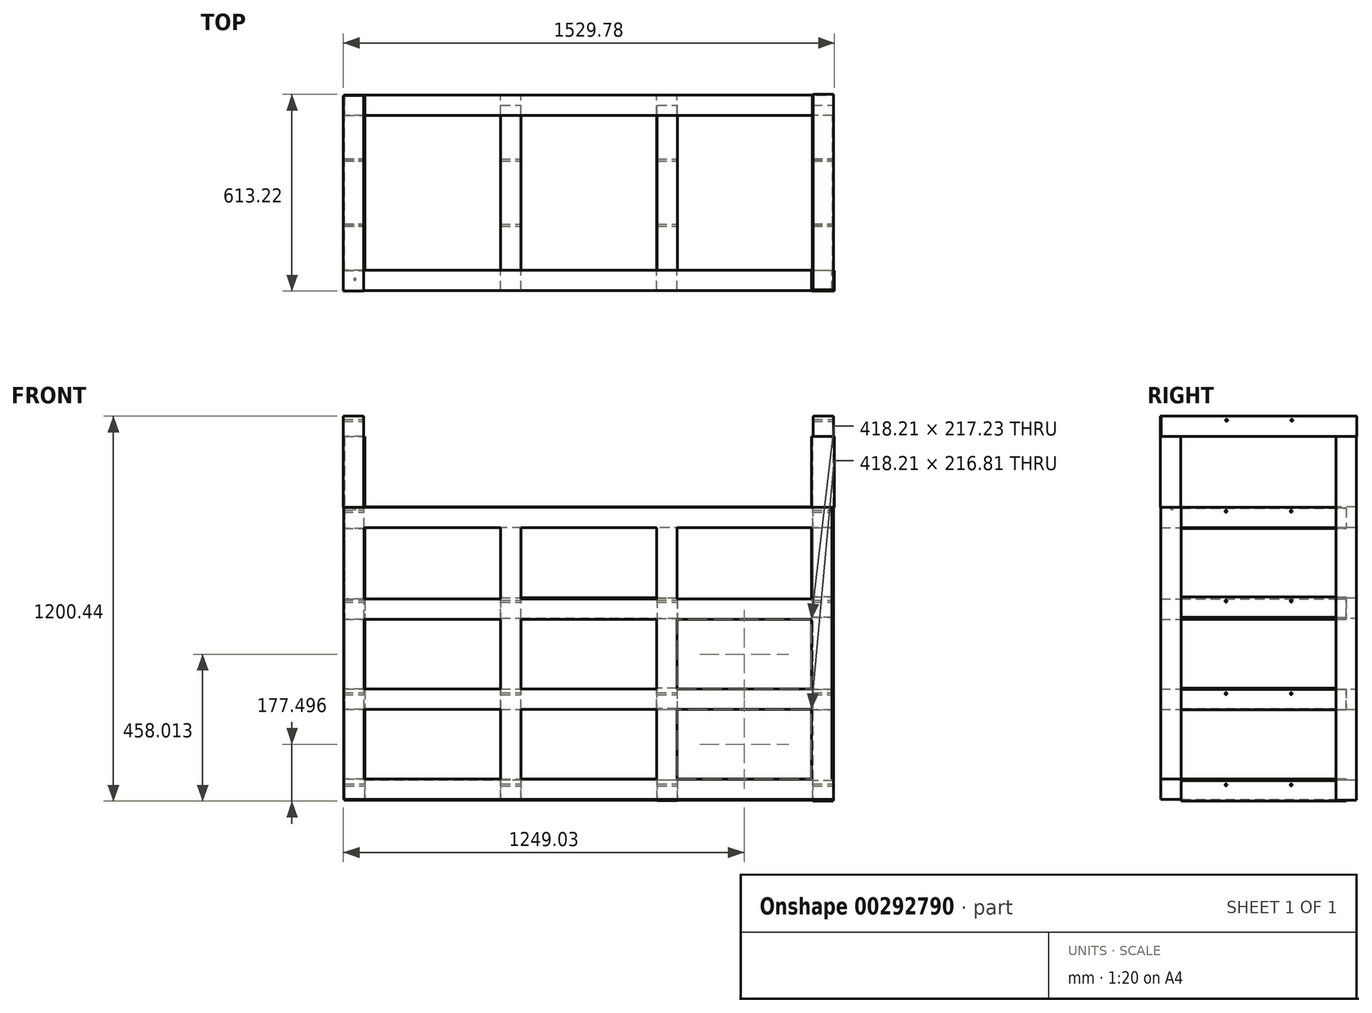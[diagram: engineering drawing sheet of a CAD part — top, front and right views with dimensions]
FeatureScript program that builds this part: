
annotation { "Feature Type Name" : "Feature", "Feature Type Description" : "" }
export const myFeature = defineFeature(function(context is Context, id is Id, definition is map)
    precondition{}
    {
        {
            var Q0;
            Q0=qCreatedBy(makeId("Front.planeOp"),FACE);
            var sketch = newSketch(context, id + "F0", { "sketchPlane" : qUnion([Q0])});
            skLineSegment(sketch, "E0.bottom", {"start": v(-550.42, 484.86) * mm, "end": v(-486.92, 484.86) * mm});
            skLineSegment(sketch, "E0.top", {"start": v(-550.42, -366.04) * mm, "end": v(-486.92, -366.04) * mm});
            skLineSegment(sketch, "E0.left", {"start": v(-550.42, 484.86) * mm, "end": v(-550.42, -366.04) * mm});
            skLineSegment(sketch, "E0.right", {"start": v(-486.92, 484.86) * mm, "end": v(-486.92, -366.04) * mm});
            skLineSegment(sketch, "E1.bottom", {"start": v(-486.92, -366.04) * mm, "end": v(910.08, -366.04) * mm});
            skLineSegment(sketch, "E1.top", {"start": v(-486.92, -302.54) * mm, "end": v(156.84, -302.54) * mm});
            skLineSegment(sketch, "E1.left", {"start": v(-486.92, -366.04) * mm, "end": v(-486.92, -302.54) * mm});
            skLineSegment(sketch, "E2.bottom", {"start": v(-550.42, 484.86) * mm, "end": v(973.58, 484.86) * mm});
            skLineSegment(sketch, "E2.top", {"start": v(-550.42, 548.36) * mm, "end": v(973.58, 548.36) * mm});
            skLineSegment(sketch, "E2.left", {"start": v(-550.42, 484.86) * mm, "end": v(-550.42, 548.36) * mm});
            skLineSegment(sketch, "E2.right", {"start": v(973.58, 484.86) * mm, "end": v(973.58, 548.36) * mm});
            skLineSegment(sketch, "E3.bottom", {"start": v(910.08, -366.04) * mm, "end": v(973.58, -366.04) * mm});
            skLineSegment(sketch, "E3.top", {"start": v(910.08, 484.86) * mm, "end": v(973.58, 484.86) * mm});
            skLineSegment(sketch, "E3.left", {"start": v(910.08, -366.04) * mm, "end": v(910.08, 484.86) * mm});
            skLineSegment(sketch, "E3.right", {"start": v(973.58, -366.04) * mm, "end": v(973.58, 484.86) * mm});
            skLineSegment(sketch, "E4", {"start": v(156.84, -302.54) * mm, "end": v(910.08, -302.54) * mm});
            skLineSegment(sketch, "E5.bottom", {"start": v(-486.92, 201.14) * mm, "end": v(910.08, 201.14) * mm});
            skLineSegment(sketch, "E5.top", {"start": v(-486.92, 264.64) * mm, "end": v(910.08, 264.64) * mm});
            skLineSegment(sketch, "E5.left", {"start": v(-486.92, 264.64) * mm, "end": v(-486.92, 201.14) * mm});
            skLineSegment(sketch, "E5.right", {"start": v(910.08, 264.64) * mm, "end": v(910.08, 201.14) * mm});
            skLineSegment(sketch, "E6.bottom", {"start": v(-486.92, -82.58) * mm, "end": v(910.08, -82.58) * mm});
            skLineSegment(sketch, "E6.top", {"start": v(-486.92, -19.08) * mm, "end": v(910.08, -19.08) * mm});
            skLineSegment(sketch, "E6.left", {"start": v(-486.92, -82.58) * mm, "end": v(-486.92, -19.08) * mm});
            skLineSegment(sketch, "E6.right", {"start": v(910.08, -82.58) * mm, "end": v(910.08, -19.08) * mm});
            skLineSegment(sketch, "E7.bottom", {"start": v(-63.5, 484.86) * mm, "end": v(0, 484.86) * mm});
            skLineSegment(sketch, "E7.top", {"start": v(-63.5, -302.54) * mm, "end": v(0, -302.54) * mm});
            skLineSegment(sketch, "E7.left", {"start": v(-63.5, 484.86) * mm, "end": v(-63.5, -302.54) * mm});
            skLineSegment(sketch, "E7.right", {"start": v(0, 484.86) * mm, "end": v(0, -302.54) * mm});
            skLineSegment(sketch, "E8.bottom", {"start": v(423.42, 484.86) * mm, "end": v(486.92, 484.86) * mm});
            skLineSegment(sketch, "E8.top", {"start": v(423.42, -302.54) * mm, "end": v(486.92, -302.54) * mm});
            skLineSegment(sketch, "E8.left", {"start": v(423.42, 484.86) * mm, "end": v(423.42, -302.54) * mm});
            skLineSegment(sketch, "E8.right", {"start": v(486.92, 484.86) * mm, "end": v(486.92, -302.54) * mm});
            skSolve(sketch);
        }
        {
            var Q0;
            Q0=makeQuery(id+"F0.imprint","IMPRINT",FACE,{"disambiguationData":[TD([[makeQuery(id+"F0.imprint","IMPRINT",EDGE,{"derivedFrom":sQuery(id+"F0.wireOp",EDGE,"E0.top")}),1.0]])]});
            var Q1;
            {var subQ0=sQuery(id+"F0.wireOp",EDGE,"E6.left");Q1=makeQuery(id+"F0.imprint","IMPRINT",FACE,{"disambiguationData":[TD([[makeQuery(id+"F0.imprint","IMPRINT",EDGE,{"derivedFrom":subQ0}),-1.0]])]});}
            var Q2;
            {var subQ0=sQuery(id+"F0.wireOp",EDGE,"E7.right");var subQ1=sQuery(id+"F0.wireOp",EDGE,"E6.bottom");var subQ2=makeQuery(id+"F0.imprint","INTERSECT",VERTEX,{"derivedFrom":[subQ1,subQ0]});Q2=makeQuery(id+"F0.imprint","IMPRINT",FACE,{"disambiguationData":[TD([[makeQuery(id+"F0.imprint","IMPRINT",EDGE,{"disambiguationData":[TD([[subQ2,-1.0]])],"derivedFrom":subQ1}),1.0]])]});}
            var Q3;
            {var subQ0=sQuery(id+"F0.wireOp",EDGE,"E6.right");Q3=makeQuery(id+"F0.imprint","IMPRINT",FACE,{"disambiguationData":[TD([[makeQuery(id+"F0.imprint","IMPRINT",EDGE,{"derivedFrom":subQ0}),1.0]])]});}
            var Q4;
            {var subQ5=sQuery(id+"F0.wireOp",EDGE,"E8.top");Q4=makeQuery(id+"F0.imprint","IMPRINT",FACE,{"disambiguationData":[TD([[makeQuery(id+"F0.imprint","IMPRINT",EDGE,{"derivedFrom":subQ5}),1.0]])]});}
            var Q5;
            {var subQ0=sQuery(id+"F0.wireOp",EDGE,"E8.left");var subQ1=sQuery(id+"F0.wireOp",EDGE,"E6.bottom");var subQ2=makeQuery(id+"F0.imprint","INTERSECT",VERTEX,{"derivedFrom":[subQ1,subQ0]});Q5=makeQuery(id+"F0.imprint","IMPRINT",FACE,{"disambiguationData":[TD([[makeQuery(id+"F0.imprint","IMPRINT",EDGE,{"disambiguationData":[TD([[subQ2,-1.0]])],"derivedFrom":subQ1}),1.0]])]});}
            var Q6;
            {var subQ0=sQuery(id+"F0.wireOp",EDGE,"E8.left");var subQ1=sQuery(id+"F0.wireOp",EDGE,"E5.bottom");var subQ2=makeQuery(id+"F0.imprint","INTERSECT",VERTEX,{"derivedFrom":[subQ1,subQ0]});Q6=makeQuery(id+"F0.imprint","IMPRINT",FACE,{"disambiguationData":[TD([[makeQuery(id+"F0.imprint","IMPRINT",EDGE,{"disambiguationData":[TD([[subQ2,-1.0]])],"derivedFrom":subQ1}),-1.0]])]});}
            var Q7;
            {var subQ0=sQuery(id+"F0.wireOp",EDGE,"E8.left");var subQ1=sQuery(id+"F0.wireOp",EDGE,"E5.bottom");var subQ2=makeQuery(id+"F0.imprint","INTERSECT",VERTEX,{"derivedFrom":[subQ1,subQ0]});Q7=makeQuery(id+"F0.imprint","IMPRINT",FACE,{"disambiguationData":[TD([[makeQuery(id+"F0.imprint","IMPRINT",EDGE,{"disambiguationData":[TD([[subQ2,-1.0]])],"derivedFrom":subQ1}),1.0]])]});}
            var Q8;
            {var subQ5=sQuery(id+"F0.wireOp",EDGE,"E8.bottom");Q8=makeQuery(id+"F0.imprint","IMPRINT",FACE,{"disambiguationData":[TD([[makeQuery(id+"F0.imprint","IMPRINT",EDGE,{"derivedFrom":subQ5}),-1.0]])]});}
            var Q9;
            {var subQ0=sQuery(id+"F0.wireOp",EDGE,"E7.right");var subQ1=sQuery(id+"F0.wireOp",EDGE,"E5.bottom");var subQ2=makeQuery(id+"F0.imprint","INTERSECT",VERTEX,{"derivedFrom":[subQ1,subQ0]});Q9=makeQuery(id+"F0.imprint","IMPRINT",FACE,{"disambiguationData":[TD([[makeQuery(id+"F0.imprint","IMPRINT",EDGE,{"disambiguationData":[TD([[subQ2,-1.0]])],"derivedFrom":subQ1}),1.0]])]});}
            var Q10;
            {var subQ5=sQuery(id+"F0.wireOp",EDGE,"E7.bottom");Q10=makeQuery(id+"F0.imprint","IMPRINT",FACE,{"disambiguationData":[TD([[makeQuery(id+"F0.imprint","IMPRINT",EDGE,{"derivedFrom":subQ5}),-1.0]])]});}
            var Q11;
            {var subQ0=sQuery(id+"F0.wireOp",EDGE,"E7.left");var subQ1=sQuery(id+"F0.wireOp",EDGE,"E5.bottom");var subQ2=makeQuery(id+"F0.imprint","INTERSECT",VERTEX,{"derivedFrom":[subQ1,subQ0]});Q11=makeQuery(id+"F0.imprint","IMPRINT",FACE,{"disambiguationData":[TD([[makeQuery(id+"F0.imprint","IMPRINT",EDGE,{"disambiguationData":[TD([[subQ2,-1.0]])],"derivedFrom":subQ1}),-1.0]])]});}
            var Q12;
            {var subQ0=sQuery(id+"F0.wireOp",EDGE,"E7.left");var subQ1=sQuery(id+"F0.wireOp",EDGE,"E6.bottom");var subQ2=makeQuery(id+"F0.imprint","INTERSECT",VERTEX,{"derivedFrom":[subQ1,subQ0]});Q12=makeQuery(id+"F0.imprint","IMPRINT",FACE,{"disambiguationData":[TD([[makeQuery(id+"F0.imprint","IMPRINT",EDGE,{"disambiguationData":[TD([[subQ2,-1.0]])],"derivedFrom":subQ1}),1.0]])]});}
            var Q13;
            {var subQ5=sQuery(id+"F0.wireOp",EDGE,"E7.top");Q13=makeQuery(id+"F0.imprint","IMPRINT",FACE,{"disambiguationData":[TD([[makeQuery(id+"F0.imprint","IMPRINT",EDGE,{"derivedFrom":subQ5}),1.0]])]});}
            var Q14;
            {var subQ0=sQuery(id+"F0.wireOp",EDGE,"E5.left");Q14=makeQuery(id+"F0.imprint","IMPRINT",FACE,{"disambiguationData":[TD([[makeQuery(id+"F0.imprint","IMPRINT",EDGE,{"derivedFrom":subQ0}),1.0]])]});}
            var Q15;
            {var subQ0=sQuery(id+"F0.wireOp",EDGE,"E7.left");var subQ1=sQuery(id+"F0.wireOp",EDGE,"E5.bottom");var subQ2=makeQuery(id+"F0.imprint","INTERSECT",VERTEX,{"derivedFrom":[subQ1,subQ0]});Q15=makeQuery(id+"F0.imprint","IMPRINT",FACE,{"disambiguationData":[TD([[makeQuery(id+"F0.imprint","IMPRINT",EDGE,{"disambiguationData":[TD([[subQ2,-1.0]])],"derivedFrom":subQ1}),1.0]])]});}
            var Q16;
            {var subQ0=sQuery(id+"F0.wireOp",EDGE,"E5.right");Q16=makeQuery(id+"F0.imprint","IMPRINT",FACE,{"disambiguationData":[TD([[makeQuery(id+"F0.imprint","IMPRINT",EDGE,{"derivedFrom":subQ0}),-1.0]])]});}
            var Q17;
            {var subQ3=sQuery(id+"F0.wireOp",EDGE,"E3.bottom");Q17=makeQuery(id+"F0.imprint","IMPRINT",FACE,{"disambiguationData":[TD([[makeQuery(id+"F0.imprint","IMPRINT",EDGE,{"derivedFrom":subQ3}),1.0]])]});}
            var Q18;
            {var subQ6=sQuery(id+"F0.wireOp",EDGE,"E1.bottom");Q18=makeQuery(id+"F0.imprint","IMPRINT",FACE,{"disambiguationData":[TD([[makeQuery(id+"F0.imprint","IMPRINT",EDGE,{"derivedFrom":subQ6}),1.0]])]});}
            extrude(context, id + "F1", {"entities" : qUnion([Q0, Q1, Q2, Q3, Q4, Q5, Q6, Q7, Q8, Q9, Q10, Q11, Q12, Q13, Q14, Q15, Q16, Q17, Q18]), "endBound" : BoundingType.SYMMETRIC, "depth" : 63.5 * mm});
        }
        {
            var Q0;
            Q0=makeQuery(id+"F0.imprint","IMPRINT",FACE,{"disambiguationData":[TD([[makeQuery(id+"F0.imprint","IMPRINT",EDGE,{"derivedFrom":sQuery(id+"F0.wireOp",EDGE,"E2.top")}),-1.0]])]});
            extrude(context, id + "F2", {"entities" : qUnion([Q0]), "operationType" : NewBodyOperationType.ADD, "endBound" : BoundingType.SYMMETRIC, "oppositeDirection" : true, "depth" : 63.5 * mm});
        }
        {
            var Q0;
            {var subQ0=sQuery(id+"F0.wireOp",EDGE,"E2.bottom");var subQ1=sQuery(id+"F0.wireOp",EDGE,"E0.right");var subQ2=makeQuery(id+"F0.imprint","INTERSECT",VERTEX,{"derivedFrom":[subQ1,subQ0]});Q0=makeQuery(id+"F0.imprint","IMPRINT",FACE,{"disambiguationData":[TD([[makeQuery(id+"F0.imprint","IMPRINT",EDGE,{"disambiguationData":[TD([[subQ2,-1.0]])],"derivedFrom":subQ1}),1.0]])]});}
            var sketch = newSketch(context, id + "F3", { "sketchPlane" : qUnion([Q0])});
            skLineSegment(sketch, "E9.bottom", {"start": v(-552.6, 544.64) * mm, "end": v(-489.1, 544.64) * mm});
            skLineSegment(sketch, "E9.top", {"start": v(-552.6, 481.14) * mm, "end": v(-489.1, 481.14) * mm});
            skLineSegment(sketch, "E9.left", {"start": v(-552.6, 544.64) * mm, "end": v(-552.6, 481.14) * mm});
            skLineSegment(sketch, "E9.right", {"start": v(-489.1, 544.64) * mm, "end": v(-489.1, 481.14) * mm});
            skLineSegment(sketch, "E10.bottom", {"start": v(-489.1, 260.92) * mm, "end": v(-552.6, 260.92) * mm});
            skLineSegment(sketch, "E10.top", {"start": v(-489.1, 197.42) * mm, "end": v(-552.6, 197.42) * mm});
            skLineSegment(sketch, "E10.left", {"start": v(-489.1, 260.92) * mm, "end": v(-489.1, 197.42) * mm});
            skLineSegment(sketch, "E10.right", {"start": v(-552.6, 260.92) * mm, "end": v(-552.6, 197.42) * mm});
            skLineSegment(sketch, "E11.bottom", {"start": v(-63.5, -82.58) * mm, "end": v(0, -82.58) * mm});
            skLineSegment(sketch, "E11.top", {"start": v(-63.5, -19.08) * mm, "end": v(0, -19.08) * mm});
            skLineSegment(sketch, "E11.left", {"start": v(-63.5, -82.58) * mm, "end": v(-63.5, -19.08) * mm});
            skLineSegment(sketch, "E11.right", {"start": v(0, -82.58) * mm, "end": v(0, -19.08) * mm});
            skLineSegment(sketch, "E12.bottom", {"start": v(-63.5, 201.14) * mm, "end": v(0, 201.14) * mm});
            skLineSegment(sketch, "E12.top", {"start": v(-63.5, 264.64) * mm, "end": v(0, 264.64) * mm});
            skLineSegment(sketch, "E12.left", {"start": v(-63.5, 201.14) * mm, "end": v(-63.5, 264.64) * mm});
            skLineSegment(sketch, "E12.right", {"start": v(0, 201.14) * mm, "end": v(0, 264.64) * mm});
            skLineSegment(sketch, "E13.bottom", {"start": v(-549.58, -363.18) * mm, "end": v(-486.08, -363.18) * mm});
            skLineSegment(sketch, "E13.top", {"start": v(-549.58, -299.68) * mm, "end": v(-486.08, -299.68) * mm});
            skLineSegment(sketch, "E13.left", {"start": v(-549.58, -363.18) * mm, "end": v(-549.58, -299.68) * mm});
            skLineSegment(sketch, "E13.right", {"start": v(-486.08, -363.18) * mm, "end": v(-486.08, -299.68) * mm});
            skLineSegment(sketch, "E14.bottom", {"start": v(-63.5, -299.68) * mm, "end": v(0, -299.68) * mm});
            skLineSegment(sketch, "E14.top", {"start": v(-63.5, -363.18) * mm, "end": v(0, -363.18) * mm});
            skLineSegment(sketch, "E14.left", {"start": v(-63.5, -299.68) * mm, "end": v(-63.5, -363.18) * mm});
            skLineSegment(sketch, "E14.right", {"start": v(0, -299.68) * mm, "end": v(0, -363.18) * mm});
            skLineSegment(sketch, "E15.bottom", {"start": v(909.19, -305.71) * mm, "end": v(972.69, -305.71) * mm});
            skLineSegment(sketch, "E15.top", {"start": v(909.19, -369.21) * mm, "end": v(972.69, -369.21) * mm});
            skLineSegment(sketch, "E15.left", {"start": v(909.19, -305.71) * mm, "end": v(909.19, -369.21) * mm});
            skLineSegment(sketch, "E15.right", {"start": v(972.69, -305.71) * mm, "end": v(972.69, -369.21) * mm});
            skLineSegment(sketch, "E16.bottom", {"start": v(909.19, 483.75) * mm, "end": v(972.69, 483.75) * mm});
            skLineSegment(sketch, "E16.top", {"start": v(909.19, 547.25) * mm, "end": v(972.69, 547.25) * mm});
            skLineSegment(sketch, "E16.left", {"start": v(909.19, 483.75) * mm, "end": v(909.19, 547.25) * mm});
            skLineSegment(sketch, "E16.right", {"start": v(972.69, 483.75) * mm, "end": v(972.69, 547.25) * mm});
            skLineSegment(sketch, "E17.bottom", {"start": v(-489.32, -19.28) * mm, "end": v(-552.82, -19.28) * mm});
            skLineSegment(sketch, "E17.top", {"start": v(-489.32, -82.78) * mm, "end": v(-552.82, -82.78) * mm});
            skLineSegment(sketch, "E17.left", {"start": v(-489.32, -19.28) * mm, "end": v(-489.32, -82.78) * mm});
            skLineSegment(sketch, "E17.right", {"start": v(-552.82, -19.28) * mm, "end": v(-552.82, -82.78) * mm});
            skLineSegment(sketch, "E18.bottom", {"start": v(486.58, -17.47) * mm, "end": v(423.42, -17.47) * mm});
            skLineSegment(sketch, "E18.top", {"start": v(486.58, -80.97) * mm, "end": v(423.42, -80.97) * mm});
            skLineSegment(sketch, "E18.left", {"start": v(486.58, -17.47) * mm, "end": v(486.58, -80.97) * mm});
            skLineSegment(sketch, "E18.right", {"start": v(423.42, -17.47) * mm, "end": v(423.42, -80.97) * mm});
            skLineSegment(sketch, "E19.bottom", {"start": v(908.2, -21.08) * mm, "end": v(971.7, -21.08) * mm});
            skLineSegment(sketch, "E19.top", {"start": v(908.2, -84.58) * mm, "end": v(971.7, -84.58) * mm});
            skLineSegment(sketch, "E19.left", {"start": v(908.2, -21.08) * mm, "end": v(908.2, -84.58) * mm});
            skLineSegment(sketch, "E19.right", {"start": v(971.7, -21.08) * mm, "end": v(971.7, -84.58) * mm});
            skLineSegment(sketch, "E20.bottom", {"start": v(424.17, -303.6) * mm, "end": v(487.67, -303.6) * mm});
            skLineSegment(sketch, "E20.top", {"start": v(424.17, -367.1) * mm, "end": v(487.67, -367.1) * mm});
            skLineSegment(sketch, "E20.left", {"start": v(424.17, -303.6) * mm, "end": v(424.17, -367.1) * mm});
            skLineSegment(sketch, "E20.right", {"start": v(487.67, -303.6) * mm, "end": v(487.67, -367.1) * mm});
            skLineSegment(sketch, "E21.bottom", {"start": v(487.12, 263.7) * mm, "end": v(423.62, 263.7) * mm});
            skLineSegment(sketch, "E21.top", {"start": v(487.12, 200.2) * mm, "end": v(423.62, 200.2) * mm});
            skLineSegment(sketch, "E21.left", {"start": v(487.12, 263.7) * mm, "end": v(487.12, 200.2) * mm});
            skLineSegment(sketch, "E21.right", {"start": v(423.62, 263.7) * mm, "end": v(423.62, 200.2) * mm});
            skLineSegment(sketch, "E22.bottom", {"start": v(908.58, 267.37) * mm, "end": v(972.08, 267.37) * mm});
            skLineSegment(sketch, "E22.top", {"start": v(908.58, 203.87) * mm, "end": v(972.08, 203.87) * mm});
            skLineSegment(sketch, "E22.left", {"start": v(908.58, 267.37) * mm, "end": v(908.58, 203.87) * mm});
            skLineSegment(sketch, "E22.right", {"start": v(972.08, 267.37) * mm, "end": v(972.08, 203.87) * mm});
            skSolve(sketch);
        }
        {
            var Q0;
            Q0 = qSketchRegion(id + "F3", true);
            extrude(context, id + "F4", {"entities" : qUnion([Q0]), "operationType" : NewBodyOperationType.ADD, "depth" : 514.35 * mm});
        }
        {
            var Q0;
            Q0=makeQuery(id+"F4.opExtrude","CAP_FACE",FACE,{"disambiguationData":[OSD([sQuery(id+"F3.wireOp",EDGE,"E10.bottom"),sQuery(id+"F3.wireOp",EDGE,"E10.top"),sQuery(id+"F3.wireOp",EDGE,"E10.left"),sQuery(id+"F3.wireOp",EDGE,"E10.right")])],"isStart":false});
            var sketch = newSketch(context, id + "F5", { "sketchPlane" : qUnion([Q0])});
            skLineSegment(sketch, "E23.bottom", {"start": v(-552.6, 197.42) * mm, "end": v(968.4, 197.42) * mm});
            skLineSegment(sketch, "E23.top", {"start": v(-552.6, 260.92) * mm, "end": v(968.4, 260.92) * mm});
            skLineSegment(sketch, "E23.left", {"start": v(-552.6, 197.42) * mm, "end": v(-552.6, 260.92) * mm});
            skLineSegment(sketch, "E23.right", {"start": v(968.4, 197.42) * mm, "end": v(968.4, 260.92) * mm});
            skLineSegment(sketch, "E24.bottom", {"start": v(-552.6, 547.51) * mm, "end": v(968.4, 547.51) * mm});
            skLineSegment(sketch, "E24.top", {"start": v(-552.6, 484.01) * mm, "end": v(968.4, 484.01) * mm});
            skLineSegment(sketch, "E24.left", {"start": v(-552.6, 547.51) * mm, "end": v(-552.6, 484.01) * mm});
            skLineSegment(sketch, "E24.right", {"start": v(968.4, 547.51) * mm, "end": v(968.4, 484.01) * mm});
            skLineSegment(sketch, "E25.bottom", {"start": v(-552.6, -83.31) * mm, "end": v(968.4, -83.31) * mm});
            skLineSegment(sketch, "E25.top", {"start": v(-552.6, -19.81) * mm, "end": v(968.4, -19.81) * mm});
            skLineSegment(sketch, "E25.left", {"start": v(-552.6, -83.31) * mm, "end": v(-552.6, -19.81) * mm});
            skLineSegment(sketch, "E25.right", {"start": v(968.4, -83.31) * mm, "end": v(968.4, -19.81) * mm});
            skLineSegment(sketch, "E26.bottom", {"start": v(-549.97, -363.62) * mm, "end": v(974.09, -363.62) * mm});
            skLineSegment(sketch, "E26.top", {"start": v(-549.97, -300.12) * mm, "end": v(974.09, -300.12) * mm});
            skLineSegment(sketch, "E26.left", {"start": v(-549.97, -363.62) * mm, "end": v(-549.97, -300.12) * mm});
            skLineSegment(sketch, "E26.right", {"start": v(974.09, -363.62) * mm, "end": v(974.09, -300.12) * mm});
            skLineSegment(sketch, "E27.bottom", {"start": v(-552.6, 547.51) * mm, "end": v(-489.1, 547.51) * mm});
            skLineSegment(sketch, "E27.top", {"start": v(-552.6, -363.62) * mm, "end": v(-489.1, -363.62) * mm});
            skLineSegment(sketch, "E27.left", {"start": v(-552.6, 547.51) * mm, "end": v(-552.6, -363.62) * mm});
            skLineSegment(sketch, "E27.right", {"start": v(-489.1, 547.51) * mm, "end": v(-489.1, -363.62) * mm});
            skLineSegment(sketch, "E28.bottom", {"start": v(-63.5, -363.62) * mm, "end": v(0, -363.62) * mm});
            skLineSegment(sketch, "E28.top", {"start": v(-63.5, 547.51) * mm, "end": v(0, 547.51) * mm});
            skLineSegment(sketch, "E28.left", {"start": v(-63.5, -363.62) * mm, "end": v(-63.5, 547.51) * mm});
            skLineSegment(sketch, "E28.right", {"start": v(0, -363.62) * mm, "end": v(0, 547.51) * mm});
            skLineSegment(sketch, "E29.bottom", {"start": v(423.2, -363.62) * mm, "end": v(486.7, -363.62) * mm});
            skLineSegment(sketch, "E29.top", {"start": v(423.2, 547.51) * mm, "end": v(486.7, 547.51) * mm});
            skLineSegment(sketch, "E29.left", {"start": v(423.2, -363.62) * mm, "end": v(423.2, 547.51) * mm});
            skLineSegment(sketch, "E29.right", {"start": v(486.7, -363.62) * mm, "end": v(486.7, 547.51) * mm});
            skLineSegment(sketch, "E30.bottom", {"start": v(904.9, -363.62) * mm, "end": v(968.4, -363.62) * mm});
            skLineSegment(sketch, "E30.top", {"start": v(904.9, 547.51) * mm, "end": v(968.4, 547.51) * mm});
            skLineSegment(sketch, "E30.left", {"start": v(904.9, -363.62) * mm, "end": v(904.9, 547.51) * mm});
            skLineSegment(sketch, "E30.right", {"start": v(968.4, -363.62) * mm, "end": v(968.4, 547.51) * mm});
            skSolve(sketch);
        }
        {
            var Q0;
            Q0 = qSketchRegion(id + "F5", true);
            var Q1;
            {var subQ0=sQuery(id+"F5.wireOp",EDGE,"E23.top");var subQ1=sQuery(id+"F5.wireOp",EDGE,"E27.right");var subQ2=makeQuery(id+"F5.imprint","INTERSECT",VERTEX,{"derivedFrom":[subQ1,subQ0]});Q1=makeQuery(id+"F5.imprint","IMPRINT",FACE,{"disambiguationData":[TD([[makeQuery(id+"F5.imprint","IMPRINT",EDGE,{"disambiguationData":[TD([[subQ2,-1.0]])],"derivedFrom":subQ1}),1.0]])]});}
            var Q2;
            {var subQ0=sQuery(id+"F5.wireOp",EDGE,"E23.bottom");var subQ1=sQuery(id+"F5.wireOp",EDGE,"E28.right");var subQ2=makeQuery(id+"F5.imprint","INTERSECT",VERTEX,{"derivedFrom":[subQ1,subQ0]});Q2=makeQuery(id+"F5.imprint","IMPRINT",FACE,{"disambiguationData":[TD([[makeQuery(id+"F5.imprint","IMPRINT",EDGE,{"disambiguationData":[TD([[subQ2,-1.0]])],"derivedFrom":subQ1}),-1.0]])]});}
            var Q3;
            {var subQ0=sQuery(id+"F5.wireOp",EDGE,"E29.right");var subQ1=sQuery(id+"F5.wireOp",EDGE,"E25.bottom");var subQ2=makeQuery(id+"F5.imprint","INTERSECT",VERTEX,{"derivedFrom":[subQ1,subQ0]});Q3=makeQuery(id+"F5.imprint","IMPRINT",FACE,{"disambiguationData":[TD([[makeQuery(id+"F5.imprint","IMPRINT",EDGE,{"disambiguationData":[TD([[subQ2,-1.0]])],"derivedFrom":subQ1}),1.0]])]});}
            var Q4;
            {var subQ0=sQuery(id+"F5.wireOp",EDGE,"E28.right");var subQ1=sQuery(id+"F5.wireOp",EDGE,"E25.bottom");var subQ2=makeQuery(id+"F5.imprint","INTERSECT",VERTEX,{"derivedFrom":[subQ1,subQ0]});Q4=makeQuery(id+"F5.imprint","IMPRINT",FACE,{"disambiguationData":[TD([[makeQuery(id+"F5.imprint","IMPRINT",EDGE,{"disambiguationData":[TD([[subQ2,-1.0]])],"derivedFrom":subQ1}),1.0]])]});}
            var Q5;
            {var subQ0=sQuery(id+"F5.wireOp",EDGE,"E27.right");var subQ1=sQuery(id+"F5.wireOp",EDGE,"E25.bottom");var subQ2=makeQuery(id+"F5.imprint","INTERSECT",VERTEX,{"derivedFrom":[subQ1,subQ0]});Q5=makeQuery(id+"F5.imprint","IMPRINT",FACE,{"disambiguationData":[TD([[makeQuery(id+"F5.imprint","IMPRINT",EDGE,{"disambiguationData":[TD([[subQ2,-1.0]])],"derivedFrom":subQ1}),1.0]])]});}
            var Q6;
            {var subQ0=sQuery(id+"F5.wireOp",EDGE,"E28.left");var subQ1=sQuery(id+"F5.wireOp",EDGE,"E25.bottom");var subQ2=makeQuery(id+"F5.imprint","INTERSECT",VERTEX,{"derivedFrom":[subQ1,subQ0]});Q6=makeQuery(id+"F5.imprint","IMPRINT",FACE,{"disambiguationData":[TD([[makeQuery(id+"F5.imprint","IMPRINT",EDGE,{"disambiguationData":[TD([[subQ2,-1.0]])],"derivedFrom":subQ1}),1.0]])]});}
            var Q7;
            {var subQ0=sQuery(id+"F5.wireOp",EDGE,"E23.bottom");var subQ1=sQuery(id+"F5.wireOp",EDGE,"E28.left");var subQ2=makeQuery(id+"F5.imprint","INTERSECT",VERTEX,{"derivedFrom":[subQ1,subQ0]});Q7=makeQuery(id+"F5.imprint","IMPRINT",FACE,{"disambiguationData":[TD([[makeQuery(id+"F5.imprint","IMPRINT",EDGE,{"disambiguationData":[TD([[subQ2,-1.0]])],"derivedFrom":subQ1}),-1.0]])]});}
            var Q8;
            {var subQ0=sQuery(id+"F5.wireOp",EDGE,"E23.bottom");var subQ1=sQuery(id+"F5.wireOp",EDGE,"E29.right");var subQ2=makeQuery(id+"F5.imprint","INTERSECT",VERTEX,{"derivedFrom":[subQ1,subQ0]});Q8=makeQuery(id+"F5.imprint","IMPRINT",FACE,{"disambiguationData":[TD([[makeQuery(id+"F5.imprint","IMPRINT",EDGE,{"disambiguationData":[TD([[subQ2,-1.0]])],"derivedFrom":subQ1}),-1.0]])]});}
            var Q9;
            {var subQ0=sQuery(id+"F5.wireOp",EDGE,"E23.bottom");var subQ1=sQuery(id+"F5.wireOp",EDGE,"E29.left");var subQ2=makeQuery(id+"F5.imprint","INTERSECT",VERTEX,{"derivedFrom":[subQ1,subQ0]});Q9=makeQuery(id+"F5.imprint","IMPRINT",FACE,{"disambiguationData":[TD([[makeQuery(id+"F5.imprint","IMPRINT",EDGE,{"disambiguationData":[TD([[subQ2,-1.0]])],"derivedFrom":subQ1}),-1.0]])]});}
            var Q10;
            {var subQ0=sQuery(id+"F5.wireOp",EDGE,"E29.left");var subQ1=sQuery(id+"F5.wireOp",EDGE,"E25.bottom");var subQ2=makeQuery(id+"F5.imprint","INTERSECT",VERTEX,{"derivedFrom":[subQ1,subQ0]});Q10=makeQuery(id+"F5.imprint","IMPRINT",FACE,{"disambiguationData":[TD([[makeQuery(id+"F5.imprint","IMPRINT",EDGE,{"disambiguationData":[TD([[subQ2,-1.0]])],"derivedFrom":subQ1}),1.0]])]});}
            var Q11;
            {var subQ0=sQuery(id+"F5.wireOp",EDGE,"E29.left");var subQ1=sQuery(id+"F5.wireOp",EDGE,"E25.bottom");var subQ2=makeQuery(id+"F5.imprint","INTERSECT",VERTEX,{"derivedFrom":[subQ1,subQ0]});Q11=makeQuery(id+"F5.imprint","IMPRINT",FACE,{"disambiguationData":[TD([[makeQuery(id+"F5.imprint","IMPRINT",EDGE,{"disambiguationData":[TD([[subQ2,-1.0]])],"derivedFrom":subQ1}),-1.0]])]});}
            var Q12;
            {var subQ0=sQuery(id+"F5.wireOp",EDGE,"E28.left");var subQ1=sQuery(id+"F5.wireOp",EDGE,"E25.bottom");var subQ2=makeQuery(id+"F5.imprint","INTERSECT",VERTEX,{"derivedFrom":[subQ1,subQ0]});Q12=makeQuery(id+"F5.imprint","IMPRINT",FACE,{"disambiguationData":[TD([[makeQuery(id+"F5.imprint","IMPRINT",EDGE,{"disambiguationData":[TD([[subQ2,-1.0]])],"derivedFrom":subQ1}),-1.0]])]});}
            var Q13;
            {var subQ0=sQuery(id+"F5.wireOp",EDGE,"E29.left");var subQ1=sQuery(id+"F5.wireOp",EDGE,"E25.top");var subQ2=makeQuery(id+"F5.imprint","INTERSECT",VERTEX,{"derivedFrom":[subQ1,subQ0]});Q13=makeQuery(id+"F5.imprint","IMPRINT",FACE,{"disambiguationData":[TD([[makeQuery(id+"F5.imprint","IMPRINT",EDGE,{"disambiguationData":[TD([[subQ2,-1.0]])],"derivedFrom":subQ1}),1.0]])]});}
            var Q14;
            {var subQ0=sQuery(id+"F5.wireOp",EDGE,"E28.left");var subQ1=sQuery(id+"F5.wireOp",EDGE,"E25.top");var subQ2=makeQuery(id+"F5.imprint","INTERSECT",VERTEX,{"derivedFrom":[subQ1,subQ0]});Q14=makeQuery(id+"F5.imprint","IMPRINT",FACE,{"disambiguationData":[TD([[makeQuery(id+"F5.imprint","IMPRINT",EDGE,{"disambiguationData":[TD([[subQ2,-1.0]])],"derivedFrom":subQ1}),1.0]])]});}
            var Q15;
            {var subQ0=sQuery(id+"F5.wireOp",EDGE,"E29.left");var subQ1=sQuery(id+"F5.wireOp",EDGE,"E24.top");var subQ2=makeQuery(id+"F5.imprint","INTERSECT",VERTEX,{"derivedFrom":[subQ1,subQ0]});Q15=makeQuery(id+"F5.imprint","IMPRINT",FACE,{"disambiguationData":[TD([[makeQuery(id+"F5.imprint","IMPRINT",EDGE,{"disambiguationData":[TD([[subQ2,-1.0]])],"derivedFrom":subQ1}),-1.0]])]});}
            var Q16;
            {var subQ0=sQuery(id+"F5.wireOp",EDGE,"E28.left");var subQ1=sQuery(id+"F5.wireOp",EDGE,"E24.top");var subQ2=makeQuery(id+"F5.imprint","INTERSECT",VERTEX,{"derivedFrom":[subQ1,subQ0]});Q16=makeQuery(id+"F5.imprint","IMPRINT",FACE,{"disambiguationData":[TD([[makeQuery(id+"F5.imprint","IMPRINT",EDGE,{"disambiguationData":[TD([[subQ2,-1.0]])],"derivedFrom":subQ1}),-1.0]])]});}
            extrude(context, id + "F6", {"entities" : qUnion([Q0, Q1, Q2, Q3, Q4, Q5, Q6, Q7, Q8, Q9, Q10, Q11, Q12, Q13, Q14, Q15, Q16]), "operationType" : NewBodyOperationType.ADD, "depth" : 63.5 * mm});
        }
        {
            var Q0;
            Q0=makeQuery(id+"F6.opExtrude","SWEPT_FACE",FACE,{"disambiguationData":[OSD([sQuery(id+"F5.wireOp",EDGE,"E24.bottom"),sQuery(id+"F5.wireOp",EDGE,"E27.bottom"),sQuery(id+"F5.wireOp",EDGE,"E28.top"),sQuery(id+"F5.wireOp",EDGE,"E29.top"),sQuery(id+"F5.wireOp",EDGE,"E30.top")])]});
            var sketch = newSketch(context, id + "F7", { "sketchPlane" : qUnion([Q0])});
            skCircle(sketch, "E31", {"center": v(-517.67, -542.93) * mm, "radius": 3.18 * mm});
            skSolve(sketch);
        }
        {
            var Q0;
            Q0=sQuery(id+"F7.wireOp",VERTEX,"E31.center");
            var Q1;
            Q1=makeQuery(id+"F1.opExtrude","SWEPT_BODY",BODY,{"disambiguationData":[OSD([sQuery(id+"F0.wireOp",EDGE,"E0.top"),sQuery(id+"F0.wireOp",EDGE,"E0.left"),sQuery(id+"F0.wireOp",EDGE,"E0.right"),sQuery(id+"F0.wireOp",EDGE,"E1.bottom"),sQuery(id+"F0.wireOp",EDGE,"E1.top"),sQuery(id+"F0.wireOp",EDGE,"E2.bottom"),sQuery(id+"F0.wireOp",EDGE,"E3.bottom"),sQuery(id+"F0.wireOp",EDGE,"E3.top"),sQuery(id+"F0.wireOp",EDGE,"E3.left"),sQuery(id+"F0.wireOp",EDGE,"E3.right"),sQuery(id+"F0.wireOp",EDGE,"E4"),sQuery(id+"F0.wireOp",EDGE,"E5.bottom"),sQuery(id+"F0.wireOp",EDGE,"E5.top"),sQuery(id+"F0.wireOp",EDGE,"E6.bottom"),sQuery(id+"F0.wireOp",EDGE,"E6.top"),sQuery(id+"F0.wireOp",EDGE,"E7.bottom"),sQuery(id+"F0.wireOp",EDGE,"E7.left"),sQuery(id+"F0.wireOp",EDGE,"E7.right"),sQuery(id+"F0.wireOp",EDGE,"E8.bottom"),sQuery(id+"F0.wireOp",EDGE,"E8.left"),sQuery(id+"F0.wireOp",EDGE,"E8.right")])]});
            hole(context, id + "F8", {"style" : HoleStyle.SIMPLE, "endStyle" : HoleEndStyle.BLIND, "holeDiameter" : 6.35 * mm, "holeDepth" : 6.35 * mm, "tappedDepth" : 12.7 * mm, "tapClearance" : 3, "locations" : qUnion([Q0]), "scope" : qUnion([Q1])});
        }
        {
            var Q0;
            Q0=makeQuery(id+"F4.opExtrude","SWEPT_FACE",FACE,{"disambiguationData":[OSD([sQuery(id+"F3.wireOp",EDGE,"E16.right")])]});
            var sketch = newSketch(context, id + "F9", { "sketchPlane" : qUnion([Q0])});
            skCircle(sketch, "E32", {"center": v(-374.65, 534.55) * mm, "radius": 3.18 * mm});
            skCircle(sketch, "E33", {"center": v(-171.45, 534.55) * mm, "radius": 3.18 * mm});
            skCircle(sketch, "E34", {"center": v(-374.65, 254.67) * mm, "radius": 3.18 * mm});
            skCircle(sketch, "E35", {"center": v(-171.45, 254.67) * mm, "radius": 3.18 * mm});
            skCircle(sketch, "E36", {"center": v(-374.65, -33.78) * mm, "radius": 3.18 * mm});
            skCircle(sketch, "E37", {"center": v(-171.45, -33.78) * mm, "radius": 3.18 * mm});
            skCircle(sketch, "E38", {"center": v(-374.65, -318.41) * mm, "radius": 3.18 * mm});
            skCircle(sketch, "E39", {"center": v(-171.45, -318.41) * mm, "radius": 3.18 * mm});
            skSolve(sketch);
        }
        {
            var Q0;
            Q0=sQuery(id+"F9.wireOp",VERTEX,"E34.center");
            var Q1;
            Q1=sQuery(id+"F9.wireOp",VERTEX,"E35.center");
            var Q2;
            Q2=sQuery(id+"F9.wireOp",VERTEX,"E32.center");
            var Q3;
            Q3=sQuery(id+"F9.wireOp",VERTEX,"E33.center");
            var Q4;
            Q4=sQuery(id+"F9.wireOp",VERTEX,"E36.center");
            var Q5;
            Q5=sQuery(id+"F9.wireOp",VERTEX,"E37.center");
            var Q6;
            Q6=sQuery(id+"F9.wireOp",VERTEX,"E38.center");
            var Q7;
            Q7=sQuery(id+"F9.wireOp",VERTEX,"E39.center");
            var Q8;
            Q8=makeQuery(id+"F1.opExtrude","SWEPT_BODY",BODY,{"disambiguationData":[OSD([sQuery(id+"F0.wireOp",EDGE,"E0.top"),sQuery(id+"F0.wireOp",EDGE,"E0.left"),sQuery(id+"F0.wireOp",EDGE,"E0.right"),sQuery(id+"F0.wireOp",EDGE,"E1.bottom"),sQuery(id+"F0.wireOp",EDGE,"E1.top"),sQuery(id+"F0.wireOp",EDGE,"E2.bottom"),sQuery(id+"F0.wireOp",EDGE,"E3.bottom"),sQuery(id+"F0.wireOp",EDGE,"E3.top"),sQuery(id+"F0.wireOp",EDGE,"E3.left"),sQuery(id+"F0.wireOp",EDGE,"E3.right"),sQuery(id+"F0.wireOp",EDGE,"E4"),sQuery(id+"F0.wireOp",EDGE,"E5.bottom"),sQuery(id+"F0.wireOp",EDGE,"E5.top"),sQuery(id+"F0.wireOp",EDGE,"E6.bottom"),sQuery(id+"F0.wireOp",EDGE,"E6.top"),sQuery(id+"F0.wireOp",EDGE,"E7.bottom"),sQuery(id+"F0.wireOp",EDGE,"E7.left"),sQuery(id+"F0.wireOp",EDGE,"E7.right"),sQuery(id+"F0.wireOp",EDGE,"E8.bottom"),sQuery(id+"F0.wireOp",EDGE,"E8.left"),sQuery(id+"F0.wireOp",EDGE,"E8.right")])]});
            hole(context, id + "F10", {"style" : HoleStyle.SIMPLE, "endStyle" : HoleEndStyle.THROUGH, "holeDiameter" : 6.35 * mm, "tappedDepth" : 12.7 * mm, "tapClearance" : 3, "locations" : qUnion([Q0, Q1, Q2, Q3, Q4, Q5, Q6, Q7]), "scope" : qUnion([Q8])});
        }
        {
            var Q0;
            Q0=makeQuery(id+"F2.opExtrude","SWEPT_FACE",FACE,{"disambiguationData":[OSD([sQuery(id+"F0.wireOp",EDGE,"E2.top")])]});
            var sketch = newSketch(context, id + "F11", { "sketchPlane" : qUnion([Q0])});
            skLineSegment(sketch, "E40.bottom", {"start": v(973.58, 31.75) * mm, "end": v(908.58, 31.75) * mm});
            skLineSegment(sketch, "E40.top", {"start": v(973.58, -31.75) * mm, "end": v(908.58, -31.75) * mm});
            skLineSegment(sketch, "E40.left", {"start": v(973.58, 31.75) * mm, "end": v(973.58, -31.75) * mm});
            skLineSegment(sketch, "E40.right", {"start": v(908.58, 31.75) * mm, "end": v(908.58, -31.75) * mm});
            skLineSegment(sketch, "E41.bottom", {"start": v(-550.42, 31.75) * mm, "end": v(-486.92, 31.75) * mm});
            skLineSegment(sketch, "E41.top", {"start": v(-550.42, -31.75) * mm, "end": v(-486.92, -31.75) * mm});
            skLineSegment(sketch, "E41.left", {"start": v(-550.42, 31.75) * mm, "end": v(-550.42, -31.75) * mm});
            skLineSegment(sketch, "E41.right", {"start": v(-486.92, 31.75) * mm, "end": v(-486.92, -31.75) * mm});
            skSolve(sketch);
        }
        {
            var Q0;
            Q0 = qSketchRegion(id + "F11", true);
            extrude(context, id + "F12", {"entities" : qUnion([Q0]), "operationType" : NewBodyOperationType.ADD, "depth" : 220.22 * mm});
        }
        {
            var Q0;
            Q0=makeQuery(id+"F7.imprint","IMPRINT",FACE,{"disambiguationData":[TD([[makeQuery(id+"F7.imprint","IMPRINT",EDGE,{"derivedFrom":sQuery(id+"F7.wireOp",EDGE,"E31")}),-1.0]])]});
            var sketch = newSketch(context, id + "F13", { "sketchPlane" : qUnion([Q0])});
            skLineSegment(sketch, "E42.bottom", {"start": v(976.56, -516.18) * mm, "end": v(904.9, -516.18) * mm});
            skLineSegment(sketch, "E42.top", {"start": v(976.56, -579.68) * mm, "end": v(904.9, -579.68) * mm});
            skLineSegment(sketch, "E42.left", {"start": v(976.56, -516.18) * mm, "end": v(976.56, -579.68) * mm});
            skLineSegment(sketch, "E42.right", {"start": v(904.9, -516.18) * mm, "end": v(904.9, -579.68) * mm});
            skLineSegment(sketch, "E43.bottom", {"start": v(-553.22, -516.09) * mm, "end": v(-489.72, -516.09) * mm});
            skLineSegment(sketch, "E43.top", {"start": v(-553.22, -579.59) * mm, "end": v(-489.72, -579.59) * mm});
            skLineSegment(sketch, "E43.left", {"start": v(-553.22, -516.09) * mm, "end": v(-553.22, -579.59) * mm});
            skLineSegment(sketch, "E43.right", {"start": v(-489.72, -516.09) * mm, "end": v(-489.72, -579.59) * mm});
            skSolve(sketch);
        }
        {
            var Q0;
            Q0 = qSketchRegion(id + "F13", true);
            extrude(context, id + "F14", {"entities" : qUnion([Q0]), "operationType" : NewBodyOperationType.ADD, "depth" : 220.22 * mm});
        }
        {
            var Q0;
            Q0=makeQuery(id+"F14.opExtrude","CAP_FACE",FACE,{"disambiguationData":[OSD([sQuery(id+"F13.wireOp",EDGE,"E43.bottom"),sQuery(id+"F13.wireOp",EDGE,"E43.top"),sQuery(id+"F13.wireOp",EDGE,"E43.left"),sQuery(id+"F13.wireOp",EDGE,"E43.right")])],"isStart":false});
            var sketch = newSketch(context, id + "F15", { "sketchPlane" : qUnion([Q0])});
            skLineSegment(sketch, "E44.bottom", {"start": v(-553.22, -579.59) * mm, "end": v(-489.72, -579.59) * mm});
            skLineSegment(sketch, "E44.top", {"start": v(-553.22, 30.01) * mm, "end": v(-489.72, 30.01) * mm});
            skLineSegment(sketch, "E44.left", {"start": v(-553.22, -579.59) * mm, "end": v(-553.22, 30.01) * mm});
            skLineSegment(sketch, "E44.right", {"start": v(-489.72, -579.59) * mm, "end": v(-489.72, 30.01) * mm});
            skLineSegment(sketch, "E45.bottom", {"start": v(910.23, 33.54) * mm, "end": v(973.73, 33.54) * mm});
            skLineSegment(sketch, "E45.top", {"start": v(910.23, -576.06) * mm, "end": v(973.73, -576.06) * mm});
            skLineSegment(sketch, "E45.left", {"start": v(910.23, 33.54) * mm, "end": v(910.23, -576.06) * mm});
            skLineSegment(sketch, "E45.right", {"start": v(973.73, 33.54) * mm, "end": v(973.73, -576.06) * mm});
            skSolve(sketch);
        }
        {
            var Q0;
            Q0 = qSketchRegion(id + "F15", true);
            extrude(context, id + "F16", {"entities" : qUnion([Q0]), "operationType" : NewBodyOperationType.ADD, "depth" : 63.5 * mm});
        }
        {
            var Q0;
            Q0=makeQuery(id+"F16.opExtrude","SWEPT_FACE",FACE,{"disambiguationData":[OSD([sQuery(id+"F15.wireOp",EDGE,"E45.right")])]});
            var sketch = newSketch(context, id + "F17", { "sketchPlane" : qUnion([Q0])});
            skCircle(sketch, "E46", {"center": v(-372.86, 818.53) * mm, "radius": 3.35 * mm});
            skCircle(sketch, "E47", {"center": v(-169.66, 818.53) * mm, "radius": 3.18 * mm});
            skSolve(sketch);
        }
        {
            var Q0;
            Q0=sQuery(id+"F17.wireOp",VERTEX,"E46.center");
            var Q1;
            Q1=sQuery(id+"F17.wireOp",VERTEX,"E47.center");
            var Q2;
            Q2=makeQuery(id+"F1.opExtrude","SWEPT_BODY",BODY,{"disambiguationData":[OSD([sQuery(id+"F0.wireOp",EDGE,"E0.top"),sQuery(id+"F0.wireOp",EDGE,"E0.left"),sQuery(id+"F0.wireOp",EDGE,"E0.right"),sQuery(id+"F0.wireOp",EDGE,"E1.bottom"),sQuery(id+"F0.wireOp",EDGE,"E1.top"),sQuery(id+"F0.wireOp",EDGE,"E2.bottom"),sQuery(id+"F0.wireOp",EDGE,"E3.bottom"),sQuery(id+"F0.wireOp",EDGE,"E3.top"),sQuery(id+"F0.wireOp",EDGE,"E3.left"),sQuery(id+"F0.wireOp",EDGE,"E3.right"),sQuery(id+"F0.wireOp",EDGE,"E4"),sQuery(id+"F0.wireOp",EDGE,"E5.bottom"),sQuery(id+"F0.wireOp",EDGE,"E5.top"),sQuery(id+"F0.wireOp",EDGE,"E6.bottom"),sQuery(id+"F0.wireOp",EDGE,"E6.top"),sQuery(id+"F0.wireOp",EDGE,"E7.bottom"),sQuery(id+"F0.wireOp",EDGE,"E7.left"),sQuery(id+"F0.wireOp",EDGE,"E7.right"),sQuery(id+"F0.wireOp",EDGE,"E8.bottom"),sQuery(id+"F0.wireOp",EDGE,"E8.left"),sQuery(id+"F0.wireOp",EDGE,"E8.right")])]});
            hole(context, id + "F18", {"style" : HoleStyle.SIMPLE, "endStyle" : HoleEndStyle.THROUGH, "holeDiameter" : 6.35 * mm, "tappedDepth" : 12.7 * mm, "tapClearance" : 3, "locations" : qUnion([Q0, Q1]), "scope" : qUnion([Q2])});
        }
    });
